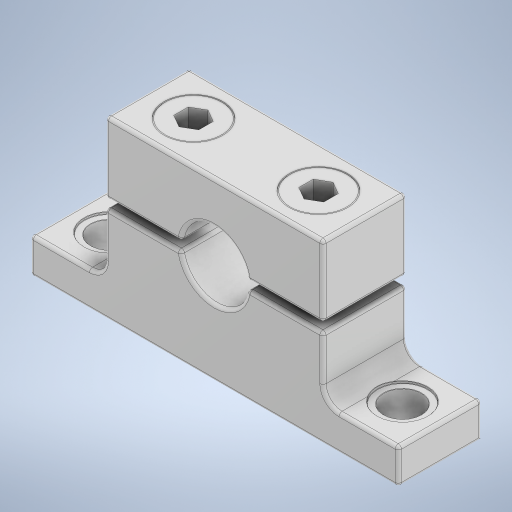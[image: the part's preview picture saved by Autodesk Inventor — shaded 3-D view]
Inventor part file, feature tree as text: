
AUTODESK INVENTOR PART (.ipt)
format: ipt  version: 2023 (Build 270158000, 158)  size: 433,152 bytes
history: mixed  units: in
note: dims shown in document units (in); Inventor stores cm internally (conversion verified against a paired STEP export)
features: fillet x2, other x1, mirror x1, imported_body x1
ambient origin geometry x8: Origin, YZ Plane, XZ Plane, XY Plane, X Axis, Y Axis, Z Axis, Center Point
bodies: Solid1 (imported_parasolid), Solid2 (imported_parasolid), Solid3 (imported_parasolid), Solid4 (imported_parasolid)
feature tree (5):
  other  "Cut-Extrude6"
  mirror  "Mirror1"
  fillet  "Fillet1"  [1 undecoded]
  fillet  "Fillet3"  [1 undecoded]
  imported_body  NMx_Import_Brep_tag  [imported B-rep: ~68 faces, bbox_mm=[32.75, 21.0, 9.238]]
note: 2 required parameter values undecoded (feature->parameter linkage not recoverable at this tier; creation-order binding heuristic only, values carry confidence <= 0.55)
